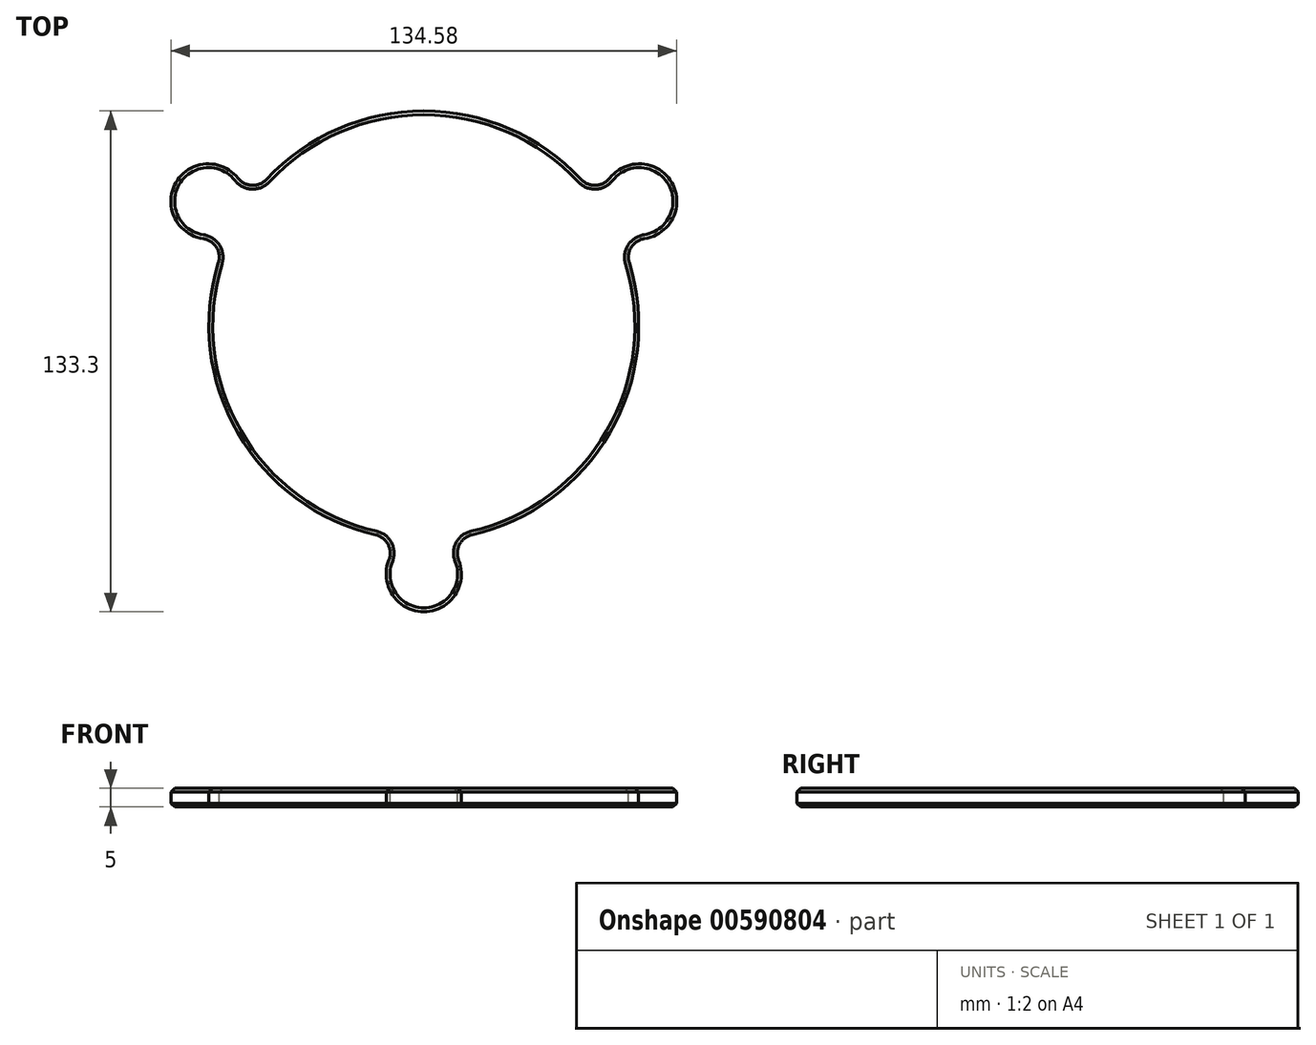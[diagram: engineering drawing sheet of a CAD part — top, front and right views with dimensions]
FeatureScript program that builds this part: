
annotation { "Feature Type Name" : "Feature", "Feature Type Description" : "" }
export const myFeature = defineFeature(function(context is Context, id is Id, definition is map)
    precondition{}
    {
        {
            var Q0;
            Q0=qCreatedBy(makeId("Top.planeOp"),FACE);
            var sketch = newSketch(context, id + "F0", { "sketchPlane" : qUnion([Q0])});
            skCircle(sketch, "E0", {"center": v(0, 0) * mm, "radius": 57.15 * mm});
            skArc(sketch, "E1", {"start": v(-4.05, -57) * mm, "mid": v(0, -76.15) * mm, "end": v(4.05, -57) * mm});
            skArc(sketch, "E2.1.0", {"start": v(51.4, 25) * mm, "mid": v(65.95, 38.07) * mm, "end": v(47.34, 32) * mm});
            skArc(sketch, "E2.2.0", {"start": v(-47.34, 32) * mm, "mid": v(-65.95, 38.08) * mm, "end": v(-51.4, 25) * mm});
            skSolve(sketch);
        }
        {
            var Q0;
            {var subQ0=sQuery(id+"F0.wireOp",EDGE,"E2.1.0");Q0=makeQuery(id+"F0.imprint","IMPRINT",FACE,{"disambiguationData":[TD([[makeQuery(id+"F0.imprint","IMPRINT",EDGE,{"derivedFrom":subQ0}),1.0]])]});}
            var Q1;
            {var subQ1=sQuery(id+"F0.wireOp",EDGE,"E0");var subQ6=sQuery(id+"F0.wireOp",EDGE,"E2.1.0");var subQ8=makeQuery(id+"F0.imprint","INTERSECT",VERTEX,{"disambiguationData":[OD(0.0)],"derivedFrom":[subQ1,subQ6]});Q1=makeQuery(id+"F0.imprint","IMPRINT",FACE,{"disambiguationData":[TD([[makeQuery(id+"F0.imprint","IMPRINT",EDGE,{"disambiguationData":[TD([[subQ8,-1.0]])],"derivedFrom":subQ1}),1.0]])]});}
            var Q2;
            {var subQ0=sQuery(id+"F0.wireOp",EDGE,"E2.2.0");Q2=makeQuery(id+"F0.imprint","IMPRINT",FACE,{"disambiguationData":[TD([[makeQuery(id+"F0.imprint","IMPRINT",EDGE,{"derivedFrom":subQ0}),1.0]])]});}
            var Q3;
            {var subQ0=sQuery(id+"F0.wireOp",EDGE,"E1");Q3=makeQuery(id+"F0.imprint","IMPRINT",FACE,{"disambiguationData":[TD([[makeQuery(id+"F0.imprint","IMPRINT",EDGE,{"derivedFrom":subQ0}),1.0]])]});}
            extrude(context, id + "F1", {"entities" : qUnion([Q0, Q1, Q2, Q3]), "depth" : 5 * mm, "offsetDistance" : 25 * mm});
        }
        {
            var Q0;
            {var subQ0=sQuery(id+"F0.wireOp",EDGE,"E1");var subQ1=sQuery(id+"F0.wireOp",EDGE,"E0");Q0=makeQuery(id+"F1.opExtrude","SWEPT_EDGE",EDGE,{"disambiguationData":[OSD([subQ1,subQ0]),TDD([makeQuery(id+"F0.imprint","INTERSECT",VERTEX,{"disambiguationData":[OD(1.0)],"derivedFrom":[subQ1,subQ0]})])]});}
            var Q1;
            {var subQ0=sQuery(id+"F0.wireOp",EDGE,"E1");var subQ1=sQuery(id+"F0.wireOp",EDGE,"E0");Q1=makeQuery(id+"F1.opExtrude","SWEPT_EDGE",EDGE,{"disambiguationData":[OSD([subQ1,subQ0]),TDD([makeQuery(id+"F0.imprint","INTERSECT",VERTEX,{"disambiguationData":[OD(0.0)],"derivedFrom":[subQ1,subQ0]})])]});}
            var Q2;
            {var subQ0=sQuery(id+"F0.wireOp",EDGE,"E2.2.0");var subQ1=sQuery(id+"F0.wireOp",EDGE,"E0");Q2=makeQuery(id+"F1.opExtrude","SWEPT_EDGE",EDGE,{"disambiguationData":[OSD([subQ1,subQ0]),TDD([makeQuery(id+"F0.imprint","INTERSECT",VERTEX,{"disambiguationData":[OD(1.0)],"derivedFrom":[subQ1,subQ0]})])]});}
            var Q3;
            {var subQ0=sQuery(id+"F0.wireOp",EDGE,"E2.2.0");var subQ1=sQuery(id+"F0.wireOp",EDGE,"E0");Q3=makeQuery(id+"F1.opExtrude","SWEPT_EDGE",EDGE,{"disambiguationData":[OSD([subQ1,subQ0]),TDD([makeQuery(id+"F0.imprint","INTERSECT",VERTEX,{"disambiguationData":[OD(0.0)],"derivedFrom":[subQ1,subQ0]})])]});}
            var Q4;
            {var subQ0=sQuery(id+"F0.wireOp",EDGE,"E2.1.0");var subQ1=sQuery(id+"F0.wireOp",EDGE,"E0");Q4=makeQuery(id+"F1.opExtrude","SWEPT_EDGE",EDGE,{"disambiguationData":[OSD([subQ1,subQ0]),TDD([makeQuery(id+"F0.imprint","INTERSECT",VERTEX,{"disambiguationData":[OD(1.0)],"derivedFrom":[subQ1,subQ0]})])]});}
            var Q5;
            {var subQ0=sQuery(id+"F0.wireOp",EDGE,"E2.1.0");var subQ1=sQuery(id+"F0.wireOp",EDGE,"E0");Q5=makeQuery(id+"F1.opExtrude","SWEPT_EDGE",EDGE,{"disambiguationData":[OSD([subQ1,subQ0]),TDD([makeQuery(id+"F0.imprint","INTERSECT",VERTEX,{"disambiguationData":[OD(0.0)],"derivedFrom":[subQ1,subQ0]})])]});}
            fillet(context, id + "F2", {"entities" : qUnion([Q0, Q1, Q2, Q3, Q4, Q5]), "radius" : 5 * mm, "tangentPropagation" : true, "allowEdgeOverflow" : false});
        }
        {
            var Q0;
            Q0=makeQuery(id+"F1.opExtrude","CAP_FACE",FACE,{"disambiguationData":[OSD([sQuery(id+"F0.wireOp",EDGE,"E0"),sQuery(id+"F0.wireOp",EDGE,"E1"),sQuery(id+"F0.wireOp",EDGE,"E2.1.0"),sQuery(id+"F0.wireOp",EDGE,"E2.2.0")])],"isStart":false});
            var Q1;
            Q1=makeQuery(id+"F1.opExtrude","CAP_FACE",FACE,{"disambiguationData":[OSD([sQuery(id+"F0.wireOp",EDGE,"E0"),sQuery(id+"F0.wireOp",EDGE,"E1"),sQuery(id+"F0.wireOp",EDGE,"E2.1.0"),sQuery(id+"F0.wireOp",EDGE,"E2.2.0")])],"isStart":true});
            chamfer(context, id + "F3", {"entities" : qUnion([Q0, Q1]), "width" : 1 * mm, "tangentPropagation" : true});
        }
    });
